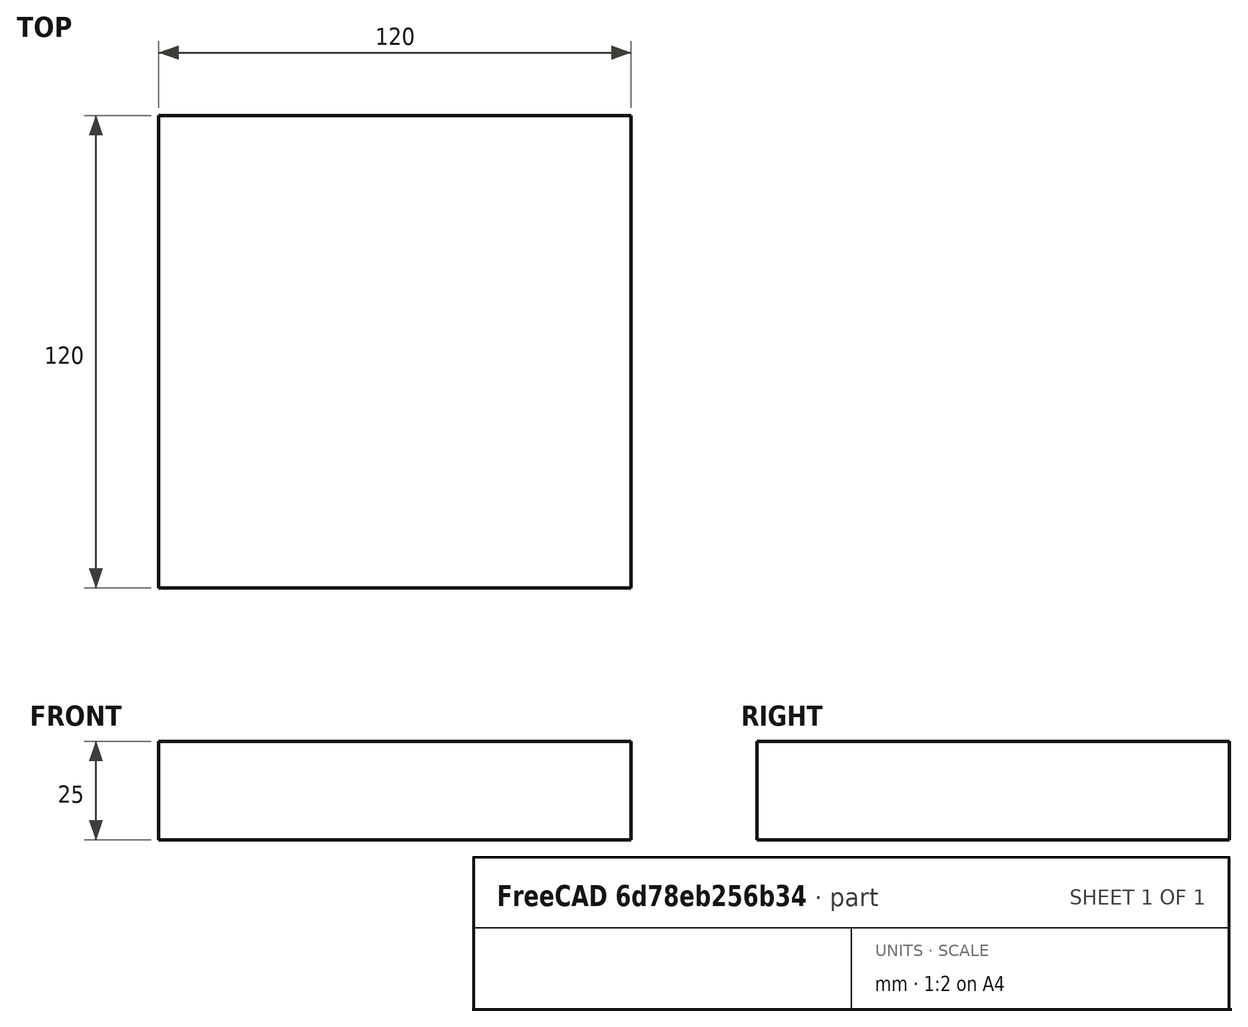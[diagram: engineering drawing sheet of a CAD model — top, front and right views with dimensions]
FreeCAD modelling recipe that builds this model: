
FCSTD DOCUMENT  (FreeCAD 0.21R33771 (Git))
Label: fan-fan
License: All rights reserved
LicenseURL: http://en.wikipedia.org/wiki/All_rights_reserved
objects: Sketcher::SketchObject×1, PartDesign::Pad×1, PartDesign::Body×1
note: 4 computed .brp shape members not serialized (recipe doc carries the construction recipe); baked Part::Feature solids carry a one-line shape summary decoded from their .brp

FEATURE [Sketcher::SketchObject] Sketch
  FullyConstrained = true
  MapMode = 5
  Support = -> [XY_Plane]
  sketch-geometry (4):
    g0: LineSegment StartX=0 StartY=0 StartZ=0 EndX=120 EndY=0 EndZ=0
    g1: LineSegment StartX=120 StartY=0 StartZ=0 EndX=120 EndY=120 EndZ=0
    g2: LineSegment StartX=120 StartY=120 StartZ=0 EndX=0 EndY=120 EndZ=0
    g3: LineSegment StartX=0 StartY=120 StartZ=0 EndX=0 EndY=0 EndZ=0
  constraints (11):
    c: Coincident(g0,g1)
    c: Coincident(g1,g2)
    c: Coincident(g2,g3)
    c: Coincident(g3,g0)
    c: Horizontal(g0)
    c: Horizontal(g2)
    c: Vertical(g1)
    c: Vertical(g3)
    c: Coincident(g0,g-1)
    c: DistanceX(g2,g2) = 120
    c: Equal(g2,g1)
FEATURE [PartDesign::Pad] Pad
  Direction = (0,0,1)
  Length = 25
  Length2 = 10
  Profile = -> Sketch
  ReferenceAxis = -> Sketch [N_Axis]
  Type = 0
FEATURE [PartDesign::Body] Body  label="实体"
  Group = -> [Sketch,Pad]
  Origin = -> Origin
  Tip = -> Pad
